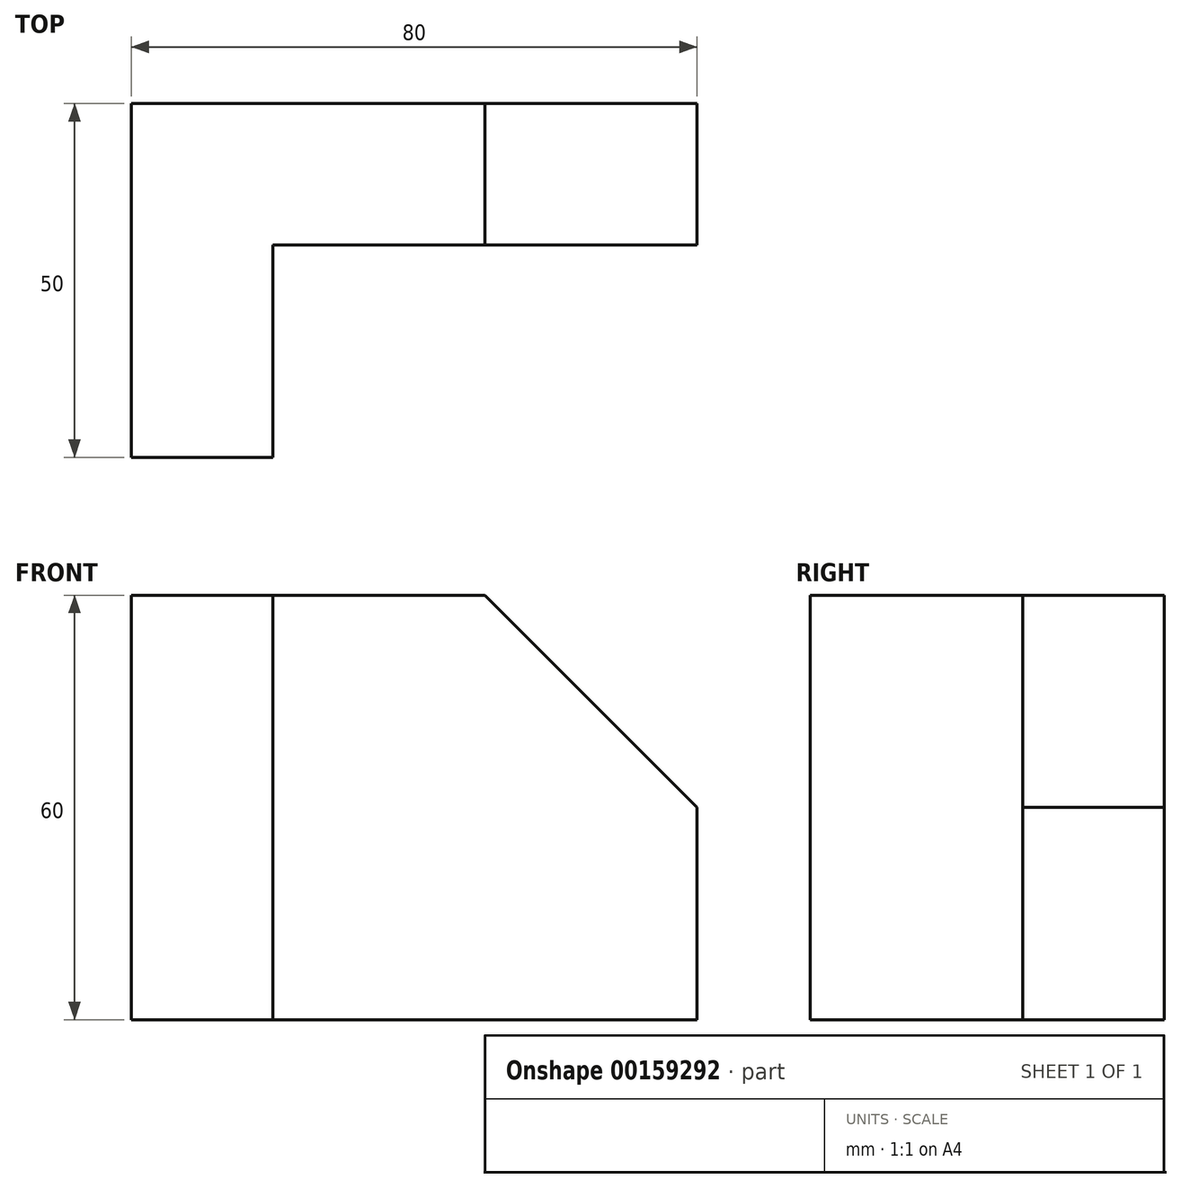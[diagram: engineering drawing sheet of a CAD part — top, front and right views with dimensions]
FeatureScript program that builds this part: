
annotation { "Feature Type Name" : "Feature", "Feature Type Description" : "" }
export const myFeature = defineFeature(function(context is Context, id is Id, definition is map)
    precondition{}
    {
        {
            var Q0;
            Q0=qCreatedBy(makeId("Front.planeOp"),FACE);
            var sketch = newSketch(context, id + "F0", { "sketchPlane" : qUnion([Q0])});
            skLineSegment(sketch, "E0.top", {"start": v(-40, -30) * mm, "end": v(40, -30) * mm});
            skLineSegment(sketch, "E0.left", {"start": v(-40, 30) * mm, "end": v(-40, -30) * mm});
            skPoint(sketch, "E0.middle", {"position": v(0, 0) * mm});
            skPoint(sketch, "E0.bottom.end.orphan", {"position": v(40, 30) * mm});
            skLineSegment(sketch, "E1", {"start": v(40, -30) * mm, "end": v(40, 0) * mm});
            skLineSegment(sketch, "E2", {"start": v(-40, 30) * mm, "end": v(10, 30) * mm});
            skLineSegment(sketch, "E3", {"start": v(10, 30) * mm, "end": v(40, 0) * mm});
            skSolve(sketch);
        }
        {
            var Q0;
            Q0 = qSketchRegion(id + "F0", true);
            extrude(context, id + "F1", {"entities" : qUnion([Q0]), "depth" : 20 * mm});
        }
        {
            var Q0;
            Q0=makeQuery(id+"F1.opExtrude","CAP_FACE",FACE,{"disambiguationData":[OSD([sQuery(id+"F0.wireOp",EDGE,"E0.top"),sQuery(id+"F0.wireOp",EDGE,"E0.left"),sQuery(id+"F0.wireOp",EDGE,"E1"),sQuery(id+"F0.wireOp",EDGE,"E2"),sQuery(id+"F0.wireOp",EDGE,"E3")])],"isStart":false});
            var sketch = newSketch(context, id + "F2", { "sketchPlane" : qUnion([Q0])});
            skLineSegment(sketch, "E4", {"start": v(-20, 30) * mm, "end": v(-20, -30) * mm});
            skLineSegment(sketch, "E5", {"start": v(-20, 30) * mm, "end": v(-40, 30) * mm});
            skLineSegment(sketch, "E6", {"start": v(-40, 30) * mm, "end": v(-40, -30) * mm});
            skLineSegment(sketch, "E7", {"start": v(-40, -30) * mm, "end": v(-20, -30) * mm});
            skSolve(sketch);
        }
        {
            var Q0;
            Q0 = qSketchRegion(id + "F2", true);
            extrude(context, id + "F3", {"entities" : qUnion([Q0]), "operationType" : NewBodyOperationType.ADD, "depth" : 30 * mm});
        }
    });
